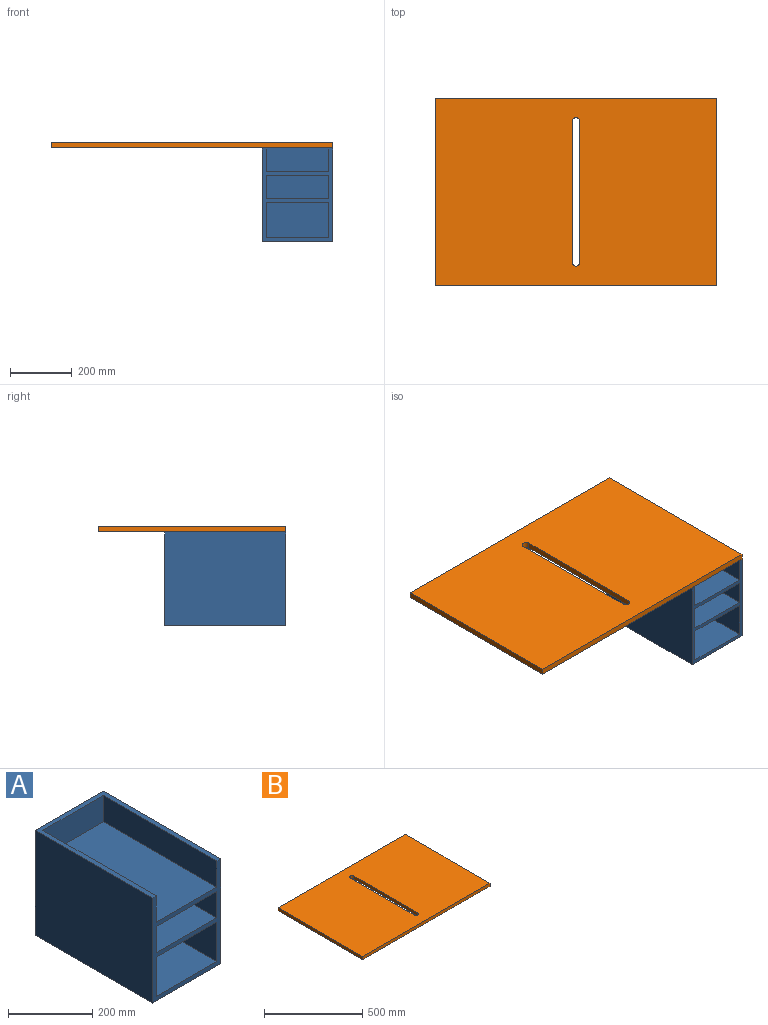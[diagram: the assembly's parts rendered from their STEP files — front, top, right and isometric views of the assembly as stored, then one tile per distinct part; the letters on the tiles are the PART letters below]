
ASSEMBLY  parts=2 mates=1
PART A: 20 faces, bbox 228.6x393.7x304.8 mm
  f0: plane 203.2x114.3mm, normal (0,-1,0), area 23225.8mm2, adj f1,f7,f13,f19
  f1: plane 381x114.3mm, normal (1,0,0), area 43548.3mm2, adj f0,f6,f7,f19
  f2: plane 381x76.2mm, normal (-1,0,0), area 29032.2mm2, adj f3,f6,f17,f18
  f3: plane 203.2x76.2mm, normal (0,-1,0), area 15483.8mm2, adj f2,f5,f17,f18
  f4: plane 381x76.2mm, normal (-1,0,0), area 29032.2mm2, adj f6,f9,f11,f16
  f5: plane 381x76.2mm, normal (1,0,0), area 29032.2mm2, adj f3,f6,f17,f18
  f6: plane 304.8x228.6mm, normal (0,-1,0), area 15483.8mm2, adj f1,f2,f4,f5,f7,f8,f9,f12
  f7: plane 381x203.2mm, normal (0,0,1), area 77419.2mm2, adj f0,f1,f6,f13
  f8: plane 393.7x228.6mm, normal (0,0,-1), area 89999.8mm2, adj f6,f10,f12,f15
  f9: plane 393.7x228.6mm, normal (0,0,1), area 12580.6mm2, adj f4,f6,f10,f11,f12,f14,f15
  f10: plane 304.8x228.6mm, normal (0,1,0), area 69677.3mm2, adj f8,f9,f12,f15
  f11: plane 203.2x76.2mm, normal (0,-1,0), area 15483.8mm2, adj f4,f9,f14,f16
  f12: plane 393.7x304.8mm, normal (1,0,0), area 119999.8mm2, adj f6,f8,f9,f10
  f13: plane 381x114.3mm, normal (-1,0,0), area 43548.3mm2, adj f0,f6,f7,f19
  f14: plane 381x76.2mm, normal (1,0,0), area 29032.2mm2, adj f6,f9,f11,f16
  f15: plane 393.7x304.8mm, normal (-1,0,0), area 119999.8mm2, adj f6,f8,f9,f10
  f16: plane 381x203.2mm, normal (0,0,1), area 77419.2mm2, adj f4,f6,f11,f14
  f17: plane 381x203.2mm, normal (0,0,-1), area 77419.2mm2, adj f2,f3,f5,f6
  f18: plane 381x203.2mm, normal (0,0,1), area 77419.2mm2, adj f2,f3,f5,f6
  f19: plane 381x203.2mm, normal (0,0,-1), area 77419.2mm2, adj f0,f1,f6,f13
PART B: 10 faces, bbox 914.4x609.6x19.1 mm
  f0: plane 914.4x19.05mm, normal (0,-1,0), area 17419.3mm2, adj f1,f3,f4,f5
  f1: plane 609.6x19.05mm, normal (1,0,0), area 11612.9mm2, adj f0,f2,f4,f5
  f2: plane 914.4x19.05mm, normal (0,1,0), area 17419.3mm2, adj f1,f3,f4,f5
  f3: plane 609.6x19.05mm, normal (-1,0,0), area 11612.9mm2, adj f0,f2,f4,f5
  f4: plane 914.4x609.6mm, normal (0,0,1), area 545298.7mm2, adj f0,f1,f2,f3,f6,f7,f8,f9
  f5: plane 914.4x609.6mm, normal (0,0,-1), area 545298.7mm2, adj f0,f1,f2,f3,f6,f7,f8,f9
  f6: plane 457.2x19.05mm, normal (-1,0,0), area 8709.7mm2, adj f4,f5,f7,f9
  f7: cylinder r=12.7mm len=25.4mm, axis (0,0,1), area 760.1mm2, adj f4,f5,f6,f8
  f8: plane 457.2x19.05mm, normal (1,0,0), area 8709.7mm2, adj f4,f5,f7,f9
  f9: cylinder r=12.7mm len=25.4mm, axis (0,0,1), area 760.1mm2, adj f4,f5,f6,f8
PLACE A t=(228.73,-166.41,-447.71)mm
PLACE B t=(-114.17,-52.11,-142.91)mm
MATE fastened B.f5 <-> A.f9  axis (0,0,-1) through (343.03,-356.91,-142.91)mm
